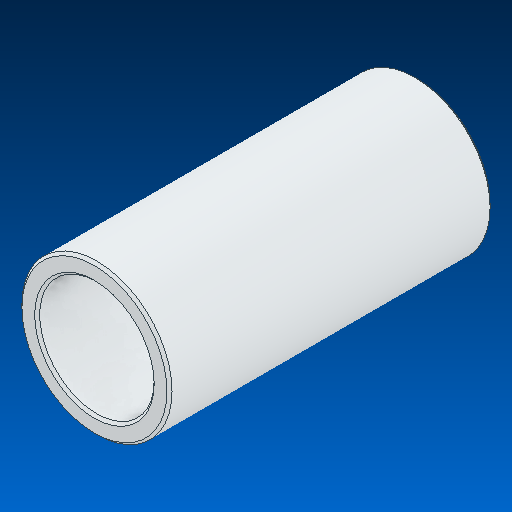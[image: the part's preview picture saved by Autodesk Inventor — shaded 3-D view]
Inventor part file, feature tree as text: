
AUTODESK INVENTOR PART (.ipt)
format: ipt  version: 2022.2 (Build 262287000, 287)  size: 122,880 bytes
history: native  units: in
note: dims shown in document units (in); Inventor stores cm internally (conversion verified against a paired STEP export)
features: chamfer x1
ambient origin geometry x8: Origin, YZ Plane, XZ Plane, XY Plane, X Axis, Y Axis, Z Axis, Center Point
bodies: Solid1 (feature_tree)
feature tree (1):
  chamfer  "Chamfer1"  [1 undecoded]
note: 1 required parameter value undecoded (feature->parameter linkage not recoverable at this tier; creation-order binding heuristic only, values carry confidence <= 0.55)
